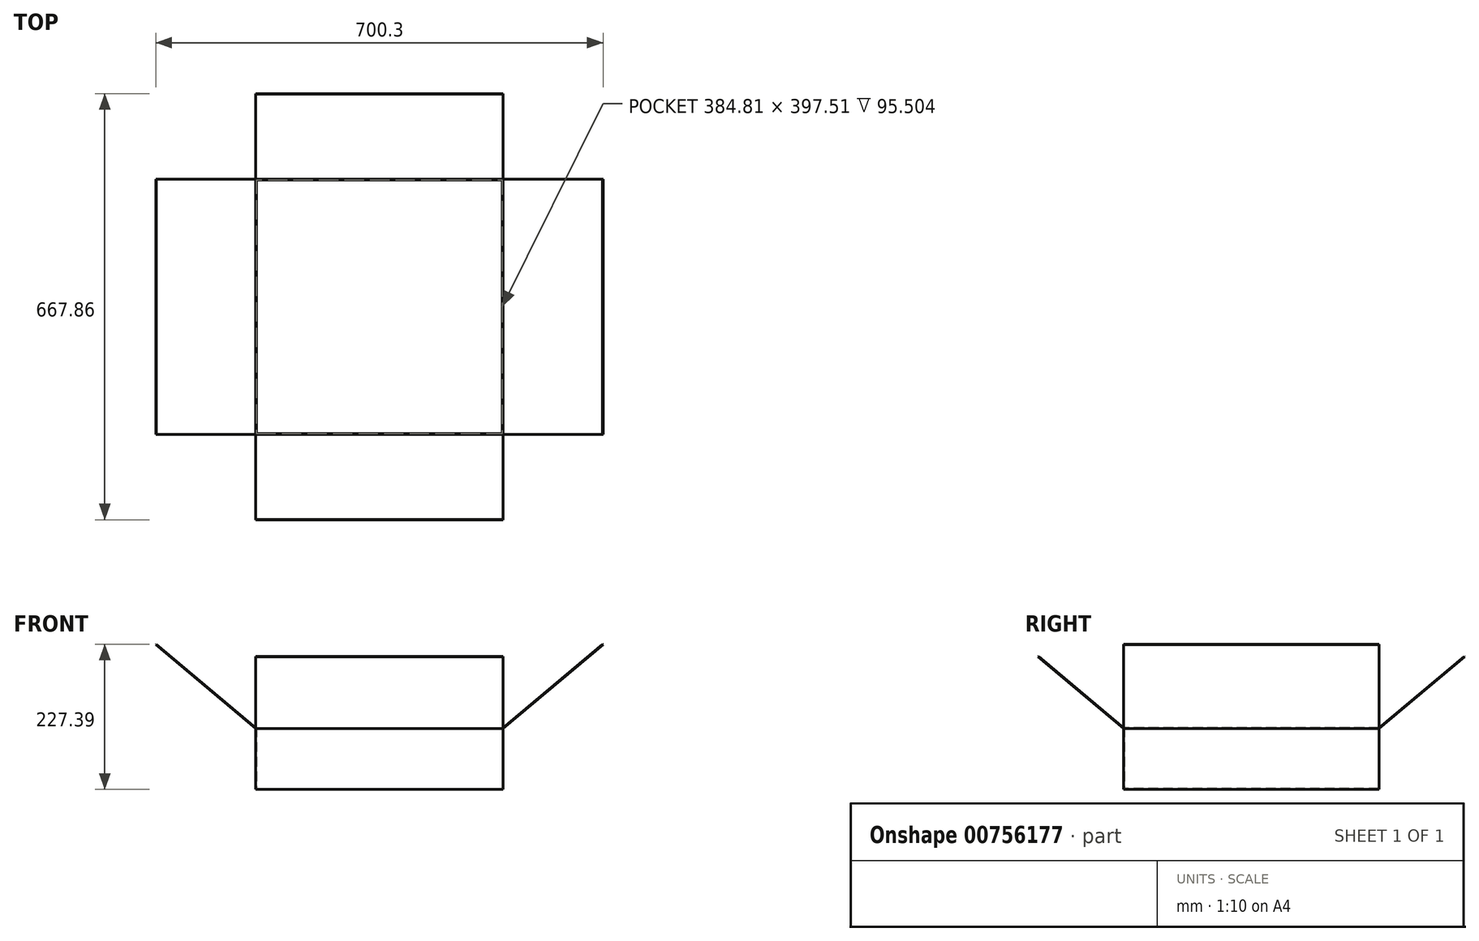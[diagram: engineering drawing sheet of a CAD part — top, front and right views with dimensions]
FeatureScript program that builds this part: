
annotation { "Feature Type Name" : "Feature", "Feature Type Description" : "" }
export const myFeature = defineFeature(function(context is Context, id is Id, definition is map)
    precondition{}
    {
        {
            var Q0;
            Q0=qCreatedBy(makeId("Top.planeOp"),FACE);
            var sketch = newSketch(context, id + "F0", { "sketchPlane" : qUnion([Q0])});
            skLineSegment(sketch, "E0.bottom", {"start": v(-100.9, 303.46) * mm, "end": v(286.44, 303.46) * mm});
            skLineSegment(sketch, "E0.top", {"start": v(-100.9, -96.59) * mm, "end": v(286.44, -96.59) * mm});
            skLineSegment(sketch, "E0.left", {"start": v(-100.9, 303.46) * mm, "end": v(-100.9, -96.59) * mm});
            skLineSegment(sketch, "E0.right", {"start": v(286.44, 303.46) * mm, "end": v(286.44, -96.59) * mm});
            skSolve(sketch);
        }
        {
            var Q0;
            Q0=makeQuery(id+"F0.imprint","IMPRINT",FACE,{"disambiguationData":[TD([[makeQuery(id+"F0.imprint","IMPRINT",EDGE,{"derivedFrom":sQuery(id+"F0.wireOp",EDGE,"E0.bottom")}),-1.0]])]});
            extrude(context, id + "F1", {"entities" : qUnion([Q0]), "depth" : 96.77 * mm, "offsetDistance" : 25.4 * mm});
        }
        {
            var Q0;
            Q0=makeQuery(id+"F1.opExtrude","CAP_FACE",FACE,{"disambiguationData":[OSD([sQuery(id+"F0.wireOp",EDGE,"E0.bottom"),sQuery(id+"F0.wireOp",EDGE,"E0.top"),sQuery(id+"F0.wireOp",EDGE,"E0.left"),sQuery(id+"F0.wireOp",EDGE,"E0.right")])],"isStart":false});
            shell(context, id + "F2", {"entities" : qUnion([Q0]), "thickness" : 1.27 * mm});
        }
        {
            var Q0;
            Q0=makeQuery(id+"F1.opExtrude","SWEPT_FACE",FACE,{"disambiguationData":[OSD([sQuery(id+"F0.wireOp",EDGE,"E0.top")])]});
            var sketch = newSketch(context, id + "F3", { "sketchPlane" : qUnion([Q0])});
            skLineSegment(sketch, "E1", {"start": v(-100.9, 96.77) * mm, "end": v(-256.57, 227.39) * mm});
            skLineSegment(sketch, "E2", {"start": v(-256.57, 227.39) * mm, "end": v(-257.38, 226.42) * mm});
            skLineSegment(sketch, "E3", {"start": v(-257.38, 226.42) * mm, "end": v(-100.9, 95.12) * mm});
            skLineSegment(sketch, "E4", {"start": v(92.77, 0) * mm, "end": v(92.77, 96.77) * mm});
            skLineSegment(sketch, "E5.MirrorCS", {"start": v(286.44, 96.77) * mm, "end": v(442.1, 227.39) * mm});
            skLineSegment(sketch, "E6.MirrorCS", {"start": v(442.1, 227.39) * mm, "end": v(442.92, 226.42) * mm});
            skLineSegment(sketch, "E7.MirrorCS", {"start": v(442.92, 226.42) * mm, "end": v(286.44, 95.12) * mm});
            skSolve(sketch);
        }
        {
            var Q0;
            {var subQ0=sQuery(id+"F3.wireOp",EDGE,"E1");Q0=makeQuery(id+"F3.imprint","IMPRINT",FACE,{"disambiguationData":[TD([[makeQuery(id+"F3.imprint","IMPRINT",EDGE,{"derivedFrom":subQ0}),1.0]])]});}
            var Q1;
            {var subQ0=sQuery(id+"F3.wireOp",EDGE,"E5.MirrorCS");Q1=makeQuery(id+"F3.imprint","IMPRINT",FACE,{"disambiguationData":[TD([[makeQuery(id+"F3.imprint","IMPRINT",EDGE,{"derivedFrom":subQ0}),-1.0]])]});}
            extrude(context, id + "F4", {"entities" : qUnion([Q0, Q1]), "operationType" : NewBodyOperationType.ADD, "oppositeDirection" : true, "depth" : 400.05 * mm, "offsetDistance" : 25.4 * mm});
        }
        {
            var Q0;
            Q0=makeQuery(id+"F1.opExtrude","SWEPT_FACE",FACE,{"disambiguationData":[OSD([sQuery(id+"F0.wireOp",EDGE,"E0.right")])]});
            var sketch = newSketch(context, id + "F5", { "sketchPlane" : qUnion([Q0])});
            skPoint(sketch, "E8.endSnap0", {"position": v(103.44, 0) * mm});
            skLineSegment(sketch, "E9", {"start": v(103.44, 0) * mm, "end": v(103.44, 95.12) * mm});
            skLineSegment(sketch, "E10", {"start": v(303.46, 96.77) * mm, "end": v(436.55, 208.45) * mm});
            skLineSegment(sketch, "E11", {"start": v(436.55, 208.45) * mm, "end": v(437.37, 207.48) * mm});
            skLineSegment(sketch, "E12", {"start": v(437.37, 207.48) * mm, "end": v(303.46, 95.12) * mm});
            skLineSegment(sketch, "E13.MirrorCS", {"start": v(-96.59, 96.77) * mm, "end": v(-229.68, 208.45) * mm});
            skLineSegment(sketch, "E14.MirrorCS", {"start": v(-230.5, 207.48) * mm, "end": v(-96.59, 95.12) * mm});
            skLineSegment(sketch, "E15.MirrorCS", {"start": v(-229.68, 208.45) * mm, "end": v(-230.5, 207.48) * mm});
            skLineSegment(sketch, "E16", {"start": v(303.46, 95.12) * mm, "end": v(303.46, 96.77) * mm});
            skLineSegment(sketch, "E17", {"start": v(-96.59, 95.12) * mm, "end": v(-96.59, 96.77) * mm});
            skSolve(sketch);
        }
        {
            var Q0;
            Q0=makeQuery(id+"F5.imprint","IMPRINT",FACE,{"disambiguationData":[TD([[makeQuery(id+"F5.imprint","IMPRINT",EDGE,{"derivedFrom":sQuery(id+"F5.wireOp",EDGE,"E10")}),-1.0]])]});
            var Q1;
            Q1=makeQuery(id+"F5.imprint","IMPRINT",FACE,{"disambiguationData":[TD([[makeQuery(id+"F5.imprint","IMPRINT",EDGE,{"derivedFrom":sQuery(id+"F5.wireOp",EDGE,"E13.MirrorCS")}),1.0]])]});
            extrude(context, id + "F6", {"entities" : qUnion([Q0, Q1]), "operationType" : NewBodyOperationType.ADD, "oppositeDirection" : true, "depth" : 387.35 * mm, "offsetDistance" : 25.4 * mm});
        }
    });
